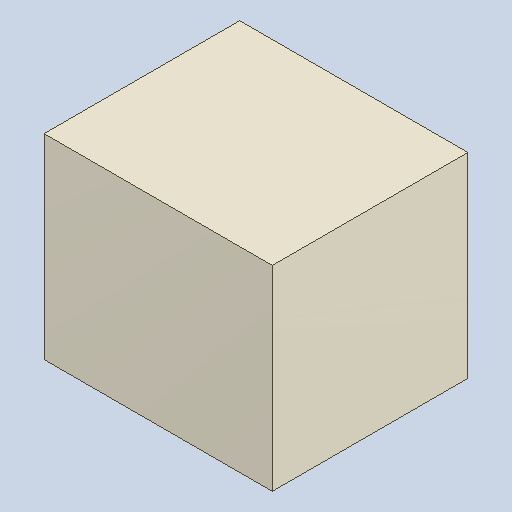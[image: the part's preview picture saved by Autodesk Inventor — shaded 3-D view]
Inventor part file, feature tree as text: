
AUTODESK INVENTOR PART (.ipt)
format: ipt  version: 2023.4 (Build 274418000, 418)  size: 82,432 bytes
history: native  units: mm
features: extrude x1
ambient origin geometry x8: Origin, YZ Plane, XZ Plane, XY Plane, X Axis, Y Axis, Z Axis, Center Point
bodies: Solid1 (feature_tree)
feature tree (1):
  extrude  "Extruded_8"  [1 undecoded]
note: 1 required parameter value undecoded (feature->parameter linkage not recoverable at this tier; creation-order binding heuristic only, values carry confidence <= 0.55)
